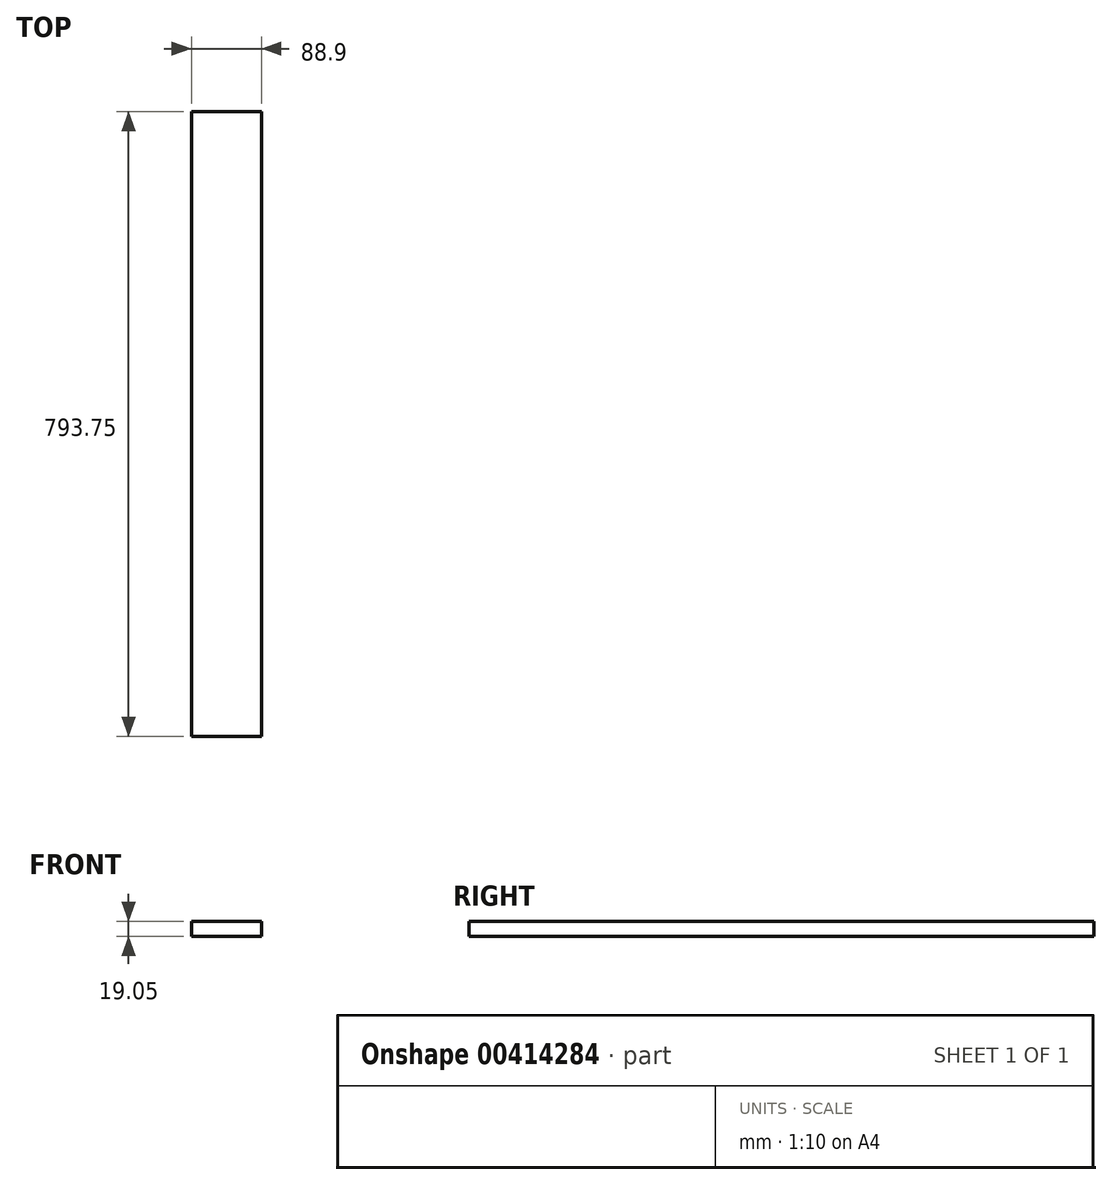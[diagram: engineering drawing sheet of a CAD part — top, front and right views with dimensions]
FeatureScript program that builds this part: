
annotation { "Feature Type Name" : "Feature", "Feature Type Description" : "" }
export const myFeature = defineFeature(function(context is Context, id is Id, definition is map)
    precondition{}
    {
        {
            var Q0;
            Q0=qCreatedBy(makeId("Front.planeOp"),FACE);
            var sketch = newSketch(context, id + "F0", { "sketchPlane" : qUnion([Q0])});
            skLineSegment(sketch, "E0.bottom", {"start": v(0, 0) * mm, "end": v(-88.9, 0) * mm});
            skLineSegment(sketch, "E0.top", {"start": v(0, 19.05) * mm, "end": v(-88.9, 19.05) * mm});
            skLineSegment(sketch, "E0.left", {"start": v(0, 0) * mm, "end": v(0, 19.05) * mm});
            skLineSegment(sketch, "E0.right", {"start": v(-88.9, 0) * mm, "end": v(-88.9, 19.05) * mm});
            skSolve(sketch);
        }
        {
            var Q0;
            Q0=qSketchRegion(id+"F0",true);
            extrude(context, id + "F1", {"entities" : qUnion([Q0]), "depth" : 793.75 * mm});
        }
    });
